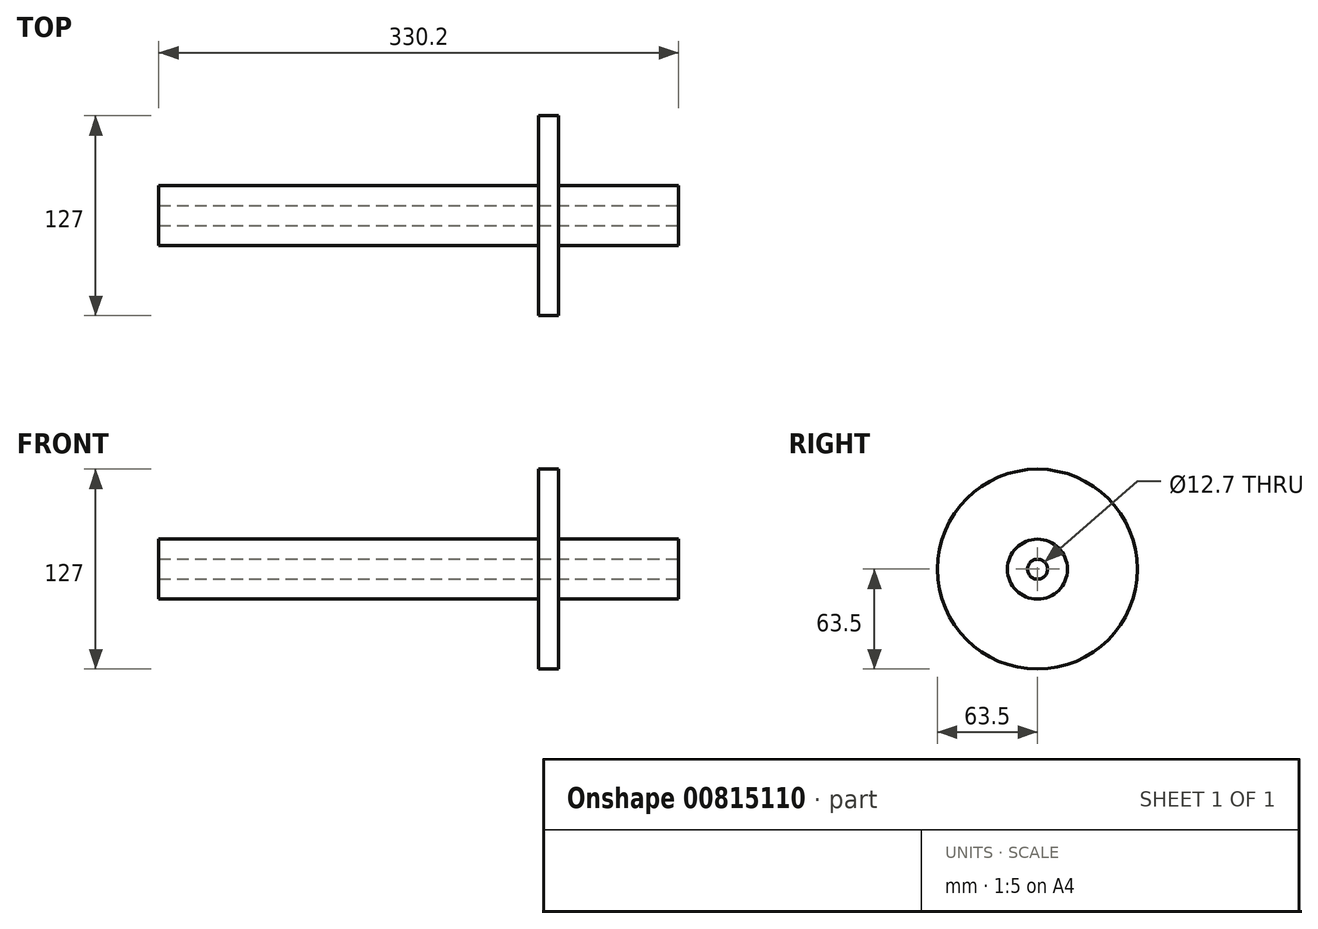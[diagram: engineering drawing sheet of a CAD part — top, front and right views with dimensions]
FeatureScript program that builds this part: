
annotation { "Feature Type Name" : "Feature", "Feature Type Description" : "" }
export const myFeature = defineFeature(function(context is Context, id is Id, definition is map)
    precondition{}
    {
        {
            var Q0;
            Q0=qCreatedBy(makeId("Right.planeOp"),FACE);
            var sketch = newSketch(context, id + "F0", { "sketchPlane" : qUnion([Q0])});
            skCircle(sketch, "E0", {"center": v(0, 0) * mm, "radius": 63.5 * mm});
            skCircle(sketch, "E1", {"center": v(0, 0) * mm, "radius": 6.35 * mm});
            skCircle(sketch, "E2", {"center": v(0, 0) * mm, "radius": 19.05 * mm});
            skSolve(sketch);
        }
        {
            var Q0;
            Q0=makeQuery(id+"F0.imprint","IMPRINT",FACE,{"disambiguationData":[TD([[makeQuery(id+"F0.imprint","IMPRINT",EDGE,{"derivedFrom":sQuery(id+"F0.wireOp",EDGE,"E1")}),-1.0]])]});
            extrude(context, id + "F1", {"entities" : qUnion([Q0]), "oppositeDirection" : true, "depth" : 254 * mm, "offsetDistance" : 25.4 * mm, "hasSecondDirection" : true, "secondDirectionOppositeDirection" : false, "secondDirectionDepth" : 76.2 * mm});
        }
        {
            var Q0;
            Q0=makeQuery(id+"F0.imprint","IMPRINT",FACE,{"disambiguationData":[TD([[makeQuery(id+"F0.imprint","IMPRINT",EDGE,{"derivedFrom":sQuery(id+"F0.wireOp",EDGE,"E0")}),1.0]])]});
            extrude(context, id + "F2", {"entities" : qUnion([Q0]), "operationType" : NewBodyOperationType.ADD, "oppositeDirection" : true, "depth" : 12.7 * mm, "offsetDistance" : 25.4 * mm});
        }
    });
